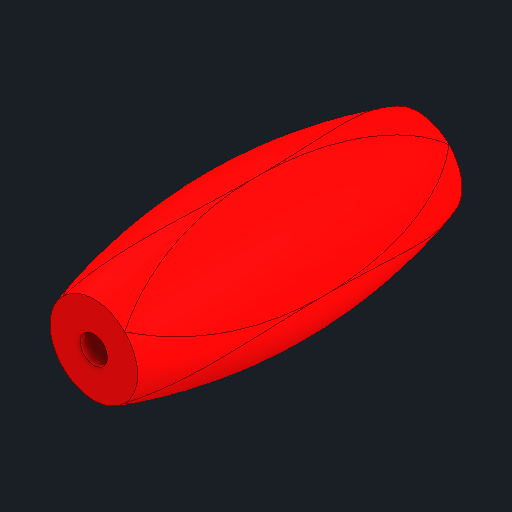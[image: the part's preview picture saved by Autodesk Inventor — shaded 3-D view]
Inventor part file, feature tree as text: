
AUTODESK INVENTOR PART (.ipt)
format: ipt  version: 2023 (Build 270158000, 158)  size: 444,928 bytes
history: native  units: mm
features: extrude x4, sketch x3, fillet x2
ambient origin geometry x8: Origin, YZ Plane, XZ Plane, XY Plane, X Axis, Y Axis, Z Axis, Center Point
bodies: Solid1 (feature_tree)
feature tree (9):
  extrude  "Extrusion1"  Depth=15.0mm
  sketch  "Sketch2"  dims[d2=3.0mm d3=35.56mm d4=0.0mm]
  sketch  "Sketch3"  dims[d5=2.0mm d6=2.0mm d7=2.0mm d8=2.0mm d9=35.56mm d10=0.0mm d11=35.56mm d12=0.0mm d13=35.56mm d14=0.0mm d15=7.499mm d16=5.0mm]
  extrude  "Extrusion2"  Depth=35.56mm TaperAngle=0.0deg
  extrude  "Extrusion3"  Depth=2.0mm
  extrude  "Extrusion4"  Depth=2.0mm
  fillet  "Fillet1"  Radius=2.0mm
  fillet  "Fillet2"  Radius=35.56mm
  sketch  "Sketch1"  dims[d0=15.0mm d1=15.0mm]
